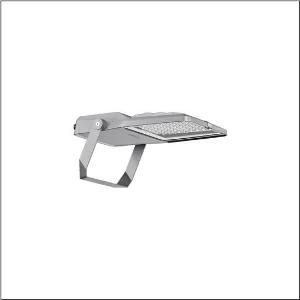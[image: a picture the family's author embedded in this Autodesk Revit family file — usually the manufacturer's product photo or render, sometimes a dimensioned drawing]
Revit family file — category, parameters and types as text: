
# Revit family: floodlight_fl_21_iq_mini___pl52_5xa7772d1d1a_9c36
name_source: partatom
category: Lighting Fixtures
units: mm (PartAtom-declared; Revit-internal decimal feet)

## family parameters
Cut with Voids When Loaded = No
Host = Face
Light Source = No
Part Type = Normal
Room Calculation Point = No
Round Connector Dimension = Use Diameter
Shared = No

## types (1)
- --- (1 x LED, 14760 lm, 143 W, 2200K)
    Apparent Load = 143 VA
    CIE Flux Codes = 26 60 98 100 100
    Color Rendering = 70
    Color Temperature = 2200K
    Default Elevation = 1800 mm
    Description = Floodlight FL 21 iQ mini, floodlight, primary light control with lens, of PMMA, primary optical cover: protective disc, of toughened safety glass, transparent, light distribution: PL52, light emission: direct distribution, installation type: surface-mounted, LED, High Power LED, rated luminous flux: 14.760lm, luminous efficacy: 103lm/W, light colour: 722, colour temperature: 2200K, control: Street-Remote, Auto-Match, Temp-Guard, Night-Set, Smart-Wire, Desk-Remote (wireless, voltage-free reading and setting of iQ features in the workshop via application-optimized NFC function/RFID function), optimised constant luminous flux control (CLO 2.0), with terminal, 6-pole, mains connection: 220..240V, AC, 50/60Hz, start of lifetime: 143W, end of service life: 152W, reduction: 61W, luminaire housing, of diecast aluminium, powder-coated, Siteco® metallic grey (DB 702S), corrosivity category C5 mid according to DIN EN ISO 12944, sealing non-destructively replaceable, mounting bracket, of steel, galvanised, powder-coated, Siteco® metallic grey (DB 702S), protection rating (complete): IP66, insulation class (complete): insulation class II (safety insulation), certification: CE, ENEC, VDE, protection symbol: D, impact resistance: IK08, permissible operating ambient temperature: -40..+40°C, permissible operating ambient temperature for outdoor applications: -40..+50°C, standard: DIN EN 12944, LABS conformity tested according to VDMA 24364:2018-05, packaging unit: 1 piece

Light Distribution: PL52
    Height = 70 mm
    Lamp = 1 x LED
    Lamp Light Flux = 14760 lm
    Lamp Power = 143 W
    Lamp count = 1
    Length = 485 mm
    Luminous efficacy = 103 lm/W
    Manufacturer = Siteco
    ModVariant = No
    Model = 5XA7772D1D1A
    Number of Poles = 1
    OnlyDefault = Yes
    Power Factor = 1
    Product Name = Floodlight FL 21 iQ mini | PL52
    Product group = floodlight | pylon annexe
    ProductGroupID = 6200
    Protection Class = Protection class II
    Protection Degree = IP 66
    RLX_Detail_Level = 1
    RLX_Emergency_Light_Flux = 0 lm
    RLX_Emergency_Type = 0
    RLX_Emergency_Type_DB = No
    RlxData = <blob elided: 96637 chars, md5=268b1cd8>
    Socket = socket
    Standby Power = 0 W
    System Light Flux = 14760 lm
    System Power = 143 W
    Type Comments = factory setting: luminous flux: 100 % | dim-lin: 254 | 730 mA
    Type Image = l_1006845.jpg
    URL = http://relux.com
    VarID = @adj_096125
    Voltage = 0 V
    Weight = 0.00 kg
    Width = 337 mm

## geometry (parser evidence)
native form markers: Blend x4, Sweep x12
no freeform markers — native parametric forms only
